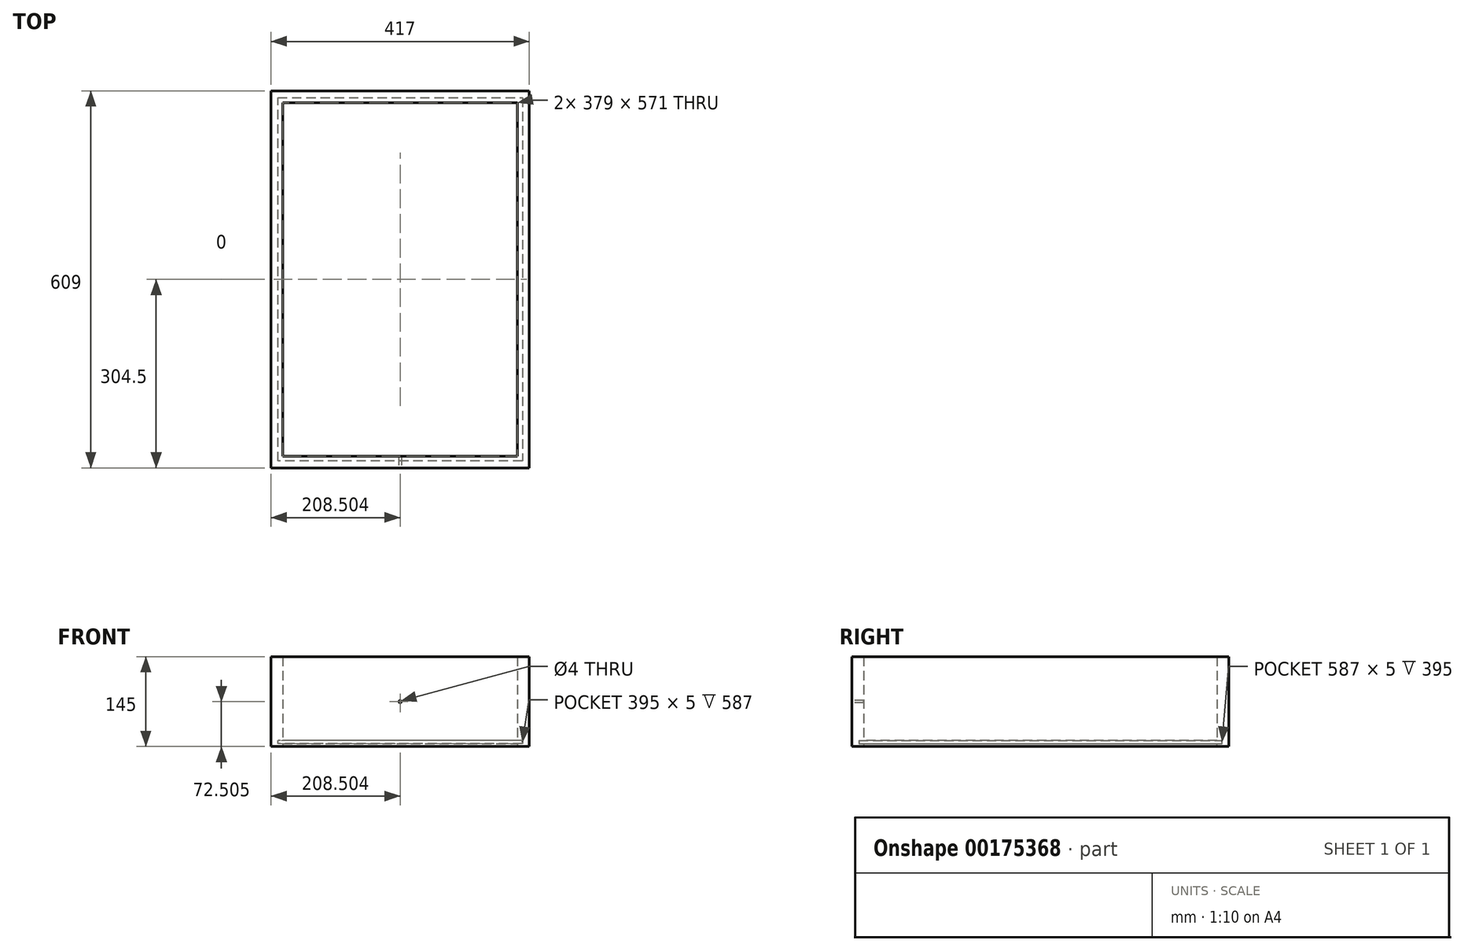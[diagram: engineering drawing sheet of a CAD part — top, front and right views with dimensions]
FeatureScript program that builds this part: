
annotation { "Feature Type Name" : "Feature", "Feature Type Description" : "" }
export const myFeature = defineFeature(function(context is Context, id is Id, definition is map)
    precondition{}
    {
        {
            var Q0;
            Q0=qCreatedBy(makeId("Front.planeOp"),FACE);
            var sketch = newSketch(context, id + "F0", { "sketchPlane" : qUnion([Q0])});
            skLineSegment(sketch, "E0.bottom", {"start": v(-224.15, 99.56) * mm, "end": v(192.85, 99.56) * mm});
            skLineSegment(sketch, "E0.top", {"start": v(-224.15, -45.44) * mm, "end": v(192.85, -45.44) * mm});
            skLineSegment(sketch, "E0.left", {"start": v(-224.15, 99.56) * mm, "end": v(-224.15, -45.44) * mm});
            skLineSegment(sketch, "E0.right", {"start": v(192.85, 99.56) * mm, "end": v(192.85, -45.44) * mm});
            skSolve(sketch);
        }
        {
            var Q0;
            Q0=makeQuery(id+"F0.imprint","IMPRINT",FACE,{"disambiguationData":[TD([[makeQuery(id+"F0.imprint","IMPRINT",EDGE,{"derivedFrom":sQuery(id+"F0.wireOp",EDGE,"E0.bottom")}),-1.0]])]});
            extrude(context, id + "F1", {"entities" : qUnion([Q0]), "depth" : 19 * mm});
        }
        {
            var Q0;
            Q0=makeQuery(id+"F1.opExtrude","CAP_FACE",FACE,{"disambiguationData":[OSD([sQuery(id+"F0.wireOp",EDGE,"E0.bottom"),sQuery(id+"F0.wireOp",EDGE,"E0.top"),sQuery(id+"F0.wireOp",EDGE,"E0.left"),sQuery(id+"F0.wireOp",EDGE,"E0.right")])],"isStart":false});
            var sketch = newSketch(context, id + "F2", { "sketchPlane" : qUnion([Q0])});
            skLineSegment(sketch, "E1.bottom", {"start": v(-224.15, -45.44) * mm, "end": v(-205.15, -45.44) * mm});
            skLineSegment(sketch, "E1.top", {"start": v(-224.15, 99.56) * mm, "end": v(-205.15, 99.56) * mm});
            skLineSegment(sketch, "E1.left", {"start": v(-224.15, -45.44) * mm, "end": v(-224.15, 99.56) * mm});
            skLineSegment(sketch, "E1.right", {"start": v(-205.15, -45.44) * mm, "end": v(-205.15, 99.56) * mm});
            skLineSegment(sketch, "E2.bottom", {"start": v(192.85, 99.56) * mm, "end": v(173.85, 99.56) * mm});
            skLineSegment(sketch, "E2.top", {"start": v(192.85, -45.44) * mm, "end": v(173.85, -45.44) * mm});
            skLineSegment(sketch, "E2.left", {"start": v(192.85, 99.56) * mm, "end": v(192.85, -45.44) * mm});
            skLineSegment(sketch, "E2.right", {"start": v(173.85, 99.56) * mm, "end": v(173.85, -45.44) * mm});
            skLineSegment(sketch, "E3.bottom", {"start": v(-205.15, -35.44) * mm, "end": v(173.85, -35.44) * mm});
            skLineSegment(sketch, "E3.top", {"start": v(-205.15, -40.44) * mm, "end": v(173.85, -40.44) * mm});
            skLineSegment(sketch, "E3.left", {"start": v(-205.15, -35.44) * mm, "end": v(-205.15, -40.44) * mm});
            skLineSegment(sketch, "E3.right", {"start": v(173.85, -35.44) * mm, "end": v(173.85, -40.44) * mm});
            skSolve(sketch);
        }
        {
            var Q0;
            {var subQ1=sQuery(id+"F2.wireOp",EDGE,"E1.bottom");Q0=makeQuery(id+"F2.imprint","IMPRINT",FACE,{"disambiguationData":[TD([[makeQuery(id+"F2.imprint","IMPRINT",EDGE,{"derivedFrom":subQ1}),1.0]])]});}
            var Q1;
            {var subQ1=sQuery(id+"F2.wireOp",EDGE,"E2.bottom");Q1=makeQuery(id+"F2.imprint","IMPRINT",FACE,{"disambiguationData":[TD([[makeQuery(id+"F2.imprint","IMPRINT",EDGE,{"derivedFrom":subQ1}),-1.0]])]});}
            extrude(context, id + "F3", {"entities" : qUnion([Q0, Q1]), "operationType" : NewBodyOperationType.ADD, "depth" : 590 * mm});
        }
        {
            var Q0;
            Q0=makeQuery(id+"F1.opExtrude","CAP_FACE",FACE,{"disambiguationData":[OSD([sQuery(id+"F0.wireOp",EDGE,"E0.bottom"),sQuery(id+"F0.wireOp",EDGE,"E0.top"),sQuery(id+"F0.wireOp",EDGE,"E0.left"),sQuery(id+"F0.wireOp",EDGE,"E0.right")])],"isStart":false});
            var sketch = newSketch(context, id + "F4", { "sketchPlane" : qUnion([Q0])});
            skLineSegment(sketch, "E4.bottom", {"start": v(-205.15, -35.44) * mm, "end": v(173.85, -35.44) * mm});
            skLineSegment(sketch, "E4.top", {"start": v(-205.15, -40.44) * mm, "end": v(173.85, -40.44) * mm});
            skLineSegment(sketch, "E4.left", {"start": v(-205.15, -35.44) * mm, "end": v(-205.15, -40.44) * mm});
            skLineSegment(sketch, "E4.right", {"start": v(173.85, -35.44) * mm, "end": v(173.85, -40.44) * mm});
            skSolve(sketch);
        }
        {
            var Q0;
            Q0=makeQuery(id+"F4.imprint","IMPRINT",FACE,{"disambiguationData":[TD([[makeQuery(id+"F4.imprint","IMPRINT",EDGE,{"derivedFrom":sQuery(id+"F4.wireOp",EDGE,"E4.bottom")}),-1.0]])]});
            extrude(context, id + "F5", {"entities" : qUnion([Q0]), "operationType" : NewBodyOperationType.REMOVE, "oppositeDirection" : true, "depth" : 8 * mm});
        }
        {
            var Q0;
            Q0=makeQuery(id+"F5.boolean.opBoolean","MERGE",FACE,{"derivedFrom":[makeQuery(id+"F3.opExtrude","SWEPT_FACE",FACE,{"disambiguationData":[OSD([sQuery(id+"F2.wireOp",EDGE,"E1.right"),sQuery(id+"F2.wireOp",EDGE,"E3.left")])]}),makeQuery(id+"F5.opExtrude","SWEPT_FACE",FACE,{"disambiguationData":[OSD([sQuery(id+"F4.wireOp",EDGE,"E4.left")])]})]});
            var sketch = newSketch(context, id + "F6", { "sketchPlane" : qUnion([Q0])});
            skLineSegment(sketch, "E5.bottom", {"start": v(-609, 99.56) * mm, "end": v(-590, 99.56) * mm});
            skLineSegment(sketch, "E5.top", {"start": v(-609, -45.44) * mm, "end": v(-590, -45.44) * mm});
            skLineSegment(sketch, "E5.left", {"start": v(-609, 99.56) * mm, "end": v(-609, -45.44) * mm});
            skLineSegment(sketch, "E5.right", {"start": v(-590, 99.56) * mm, "end": v(-590, -45.44) * mm});
            skSolve(sketch);
        }
        {
            var Q0;
            Q0=makeQuery(id+"F6.imprint","IMPRINT",FACE,{"disambiguationData":[TD([[makeQuery(id+"F6.imprint","IMPRINT",EDGE,{"derivedFrom":sQuery(id+"F6.wireOp",EDGE,"E5.bottom")}),-1.0]])]});
            extrude(context, id + "F7", {"entities" : qUnion([Q0]), "operationType" : NewBodyOperationType.ADD, "depth" : 379 * mm});
        }
        {
            var Q0;
            Q0=makeQuery(id+"F5.boolean.opBoolean","MERGE",FACE,{"derivedFrom":[makeQuery(id+"F3.opExtrude","SWEPT_FACE",FACE,{"disambiguationData":[OSD([sQuery(id+"F2.wireOp",EDGE,"E2.right"),sQuery(id+"F2.wireOp",EDGE,"E3.right")])]}),makeQuery(id+"F5.opExtrude","SWEPT_FACE",FACE,{"disambiguationData":[OSD([sQuery(id+"F4.wireOp",EDGE,"E4.right")])]})]});
            var sketch = newSketch(context, id + "F8", { "sketchPlane" : qUnion([Q0])});
            skLineSegment(sketch, "E6.bottom", {"start": v(11, -35.44) * mm, "end": v(590, -35.44) * mm});
            skLineSegment(sketch, "E6.top", {"start": v(11, -40.44) * mm, "end": v(590, -40.44) * mm});
            skLineSegment(sketch, "E6.left", {"start": v(11, -35.44) * mm, "end": v(11, -40.44) * mm});
            skLineSegment(sketch, "E6.right", {"start": v(590, -35.44) * mm, "end": v(590, -40.44) * mm});
            skSolve(sketch);
        }
        {
            var Q0;
            {var subQ10=sQuery(id+"F8.wireOp",EDGE,"E6.left");Q0=makeQuery(id+"F8.imprint","IMPRINT",FACE,{"disambiguationData":[TD([[makeQuery(id+"F8.imprint","IMPRINT",EDGE,{"derivedFrom":subQ10}),1.0]])]});}
            extrude(context, id + "F9", {"entities" : qUnion([Q0]), "operationType" : NewBodyOperationType.REMOVE, "oppositeDirection" : true, "depth" : 8 * mm});
        }
        {
            var Q0;
            Q0=makeQuery(id+"F9.boolean.opBoolean","MERGE",FACE,{"derivedFrom":[makeQuery(id+"F7.opExtrude","SWEPT_FACE",FACE,{"disambiguationData":[OSD([sQuery(id+"F6.wireOp",EDGE,"E5.right")])]}),makeQuery(id+"F9.opExtrude","SWEPT_FACE",FACE,{"disambiguationData":[OSD([sQuery(id+"F8.wireOp",EDGE,"E6.right")])]})]});
            var sketch = newSketch(context, id + "F10", { "sketchPlane" : qUnion([Q0])});
            skLineSegment(sketch, "E7.bottom", {"start": v(-181.85, -35.44) * mm, "end": v(205.15, -35.44) * mm});
            skLineSegment(sketch, "E7.top", {"start": v(-181.85, -40.44) * mm, "end": v(205.15, -40.44) * mm});
            skLineSegment(sketch, "E7.left", {"start": v(-181.85, -35.44) * mm, "end": v(-181.85, -40.44) * mm});
            skLineSegment(sketch, "E7.right", {"start": v(205.15, -35.44) * mm, "end": v(205.15, -40.44) * mm});
            skSolve(sketch);
        }
        {
            var Q0;
            {var subQ8=sQuery(id+"F10.wireOp",EDGE,"E7.left");Q0=makeQuery(id+"F10.imprint","IMPRINT",FACE,{"disambiguationData":[TD([[makeQuery(id+"F10.imprint","IMPRINT",EDGE,{"derivedFrom":subQ8}),1.0]])]});}
            extrude(context, id + "F11", {"entities" : qUnion([Q0]), "operationType" : NewBodyOperationType.REMOVE, "oppositeDirection" : true, "depth" : 8 * mm});
        }
        {
            var Q0;
            Q0=makeQuery(id+"F11.boolean.opBoolean","MERGE",FACE,{"derivedFrom":[makeQuery(id+"F5.boolean.opBoolean","MERGE",FACE,{"derivedFrom":[makeQuery(id+"F3.opExtrude","SWEPT_FACE",FACE,{"disambiguationData":[OSD([sQuery(id+"F2.wireOp",EDGE,"E1.right"),sQuery(id+"F2.wireOp",EDGE,"E3.left")])]}),makeQuery(id+"F5.opExtrude","SWEPT_FACE",FACE,{"disambiguationData":[OSD([sQuery(id+"F4.wireOp",EDGE,"E4.left")])]})]}),makeQuery(id+"F11.opExtrude","SWEPT_FACE",FACE,{"disambiguationData":[OSD([sQuery(id+"F10.wireOp",EDGE,"E7.right")])]})]});
            var sketch = newSketch(context, id + "F12", { "sketchPlane" : qUnion([Q0])});
            skLineSegment(sketch, "E8.bottom", {"start": v(-598, -35.44) * mm, "end": v(-11, -35.44) * mm});
            skLineSegment(sketch, "E8.top", {"start": v(-598, -40.44) * mm, "end": v(-11, -40.44) * mm});
            skLineSegment(sketch, "E8.left", {"start": v(-598, -35.44) * mm, "end": v(-598, -40.44) * mm});
            skLineSegment(sketch, "E8.right", {"start": v(-11, -35.44) * mm, "end": v(-11, -40.44) * mm});
            skSolve(sketch);
        }
        {
            var Q0;
            {var subQ20=sQuery(id+"F12.wireOp",EDGE,"E8.left");Q0=makeQuery(id+"F12.imprint","IMPRINT",FACE,{"disambiguationData":[TD([[makeQuery(id+"F12.imprint","IMPRINT",EDGE,{"derivedFrom":subQ20}),1.0]])]});}
            extrude(context, id + "F13", {"entities" : qUnion([Q0]), "operationType" : NewBodyOperationType.REMOVE, "oppositeDirection" : true, "depth" : 8 * mm});
        }
        {
            var Q0;
            Q0=makeQuery(id+"F7.boolean.opBoolean","MERGE",FACE,{"derivedFrom":[makeQuery(id+"F3.opExtrude","CAP_FACE",FACE,{"disambiguationData":[OSD([sQuery(id+"F2.wireOp",EDGE,"E1.bottom"),sQuery(id+"F2.wireOp",EDGE,"E1.top"),sQuery(id+"F2.wireOp",EDGE,"E1.left"),sQuery(id+"F2.wireOp",EDGE,"E1.right"),sQuery(id+"F2.wireOp",EDGE,"E3.left")])],"isStart":false}),makeQuery(id+"F3.opExtrude","CAP_FACE",FACE,{"disambiguationData":[OSD([sQuery(id+"F2.wireOp",EDGE,"E2.bottom"),sQuery(id+"F2.wireOp",EDGE,"E2.top"),sQuery(id+"F2.wireOp",EDGE,"E2.left"),sQuery(id+"F2.wireOp",EDGE,"E2.right"),sQuery(id+"F2.wireOp",EDGE,"E3.right")])],"isStart":false}),makeQuery(id+"F7.opExtrude","SWEPT_FACE",FACE,{"disambiguationData":[OSD([sQuery(id+"F6.wireOp",EDGE,"E5.left")])]})]});
            var sketch = newSketch(context, id + "F14", { "sketchPlane" : qUnion([Q0])});
            skCircle(sketch, "E9", {"center": v(-15.65, 27.06) * mm, "radius": 2 * mm});
            skPoint(sketch, "E9.centerSnap0", {"position": v(-15.65, 99.56) * mm});
            skPoint(sketch, "E9.centerSnap1", {"position": v(-224.15, 27.06) * mm});
            skSolve(sketch);
        }
        {
            var Q0;
            Q0 = qSketchRegion(id + "F14", true);
            extrude(context, id + "F15", {"entities" : qUnion([Q0]), "operationType" : NewBodyOperationType.REMOVE, "oppositeDirection" : true, "depth" : 19 * mm});
        }
    });
